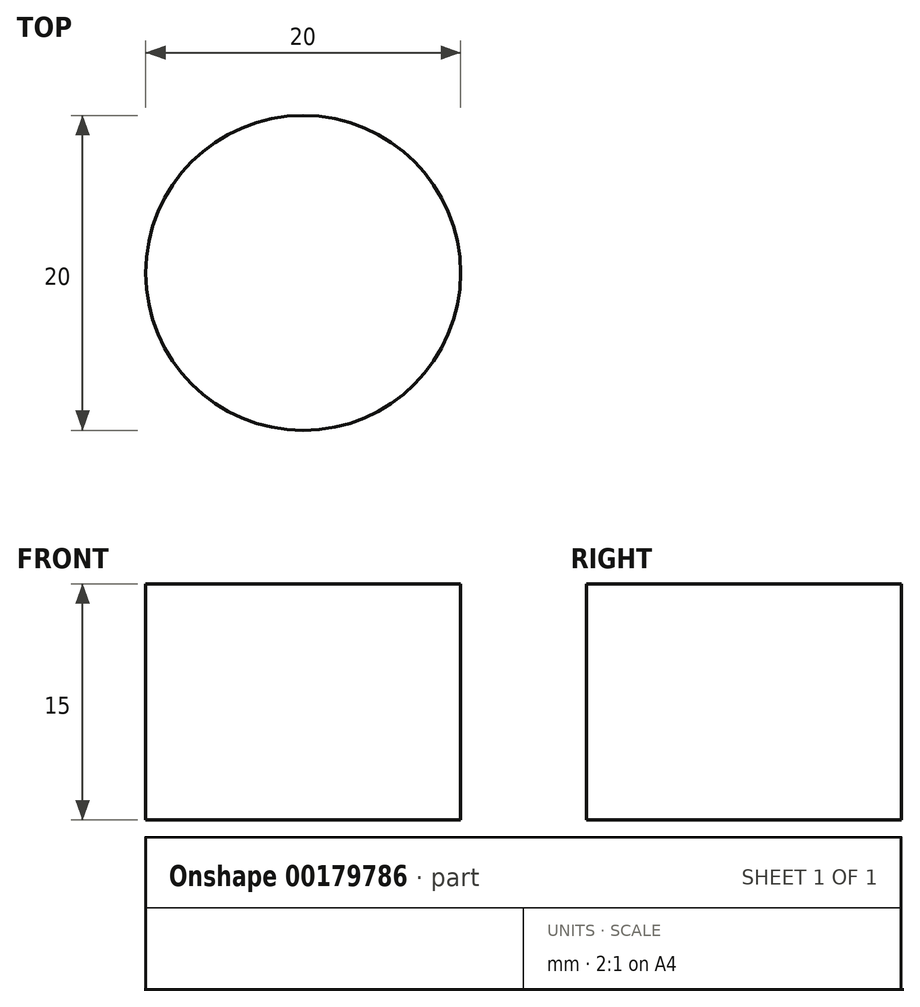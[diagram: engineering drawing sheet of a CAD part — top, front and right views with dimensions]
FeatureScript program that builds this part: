
annotation { "Feature Type Name" : "Feature", "Feature Type Description" : "" }
export const myFeature = defineFeature(function(context is Context, id is Id, definition is map)
    precondition{}
    {
        {
            var Q0;
            Q0=qCreatedBy(makeId("Top.planeOp"),FACE);
            var sketch = newSketch(context, id + "F0", { "sketchPlane" : qUnion([Q0])});
            skCircle(sketch, "E0", {"center": v(0, 0) * mm, "radius": 10 * mm});
            skSolve(sketch);
        }
        {
            var Q0;
            Q0 = qSketchRegion(id + "F0", true);
            extrude(context, id + "F1", {"entities" : qUnion([Q0]), "depth" : 15 * mm});
        }
    });
